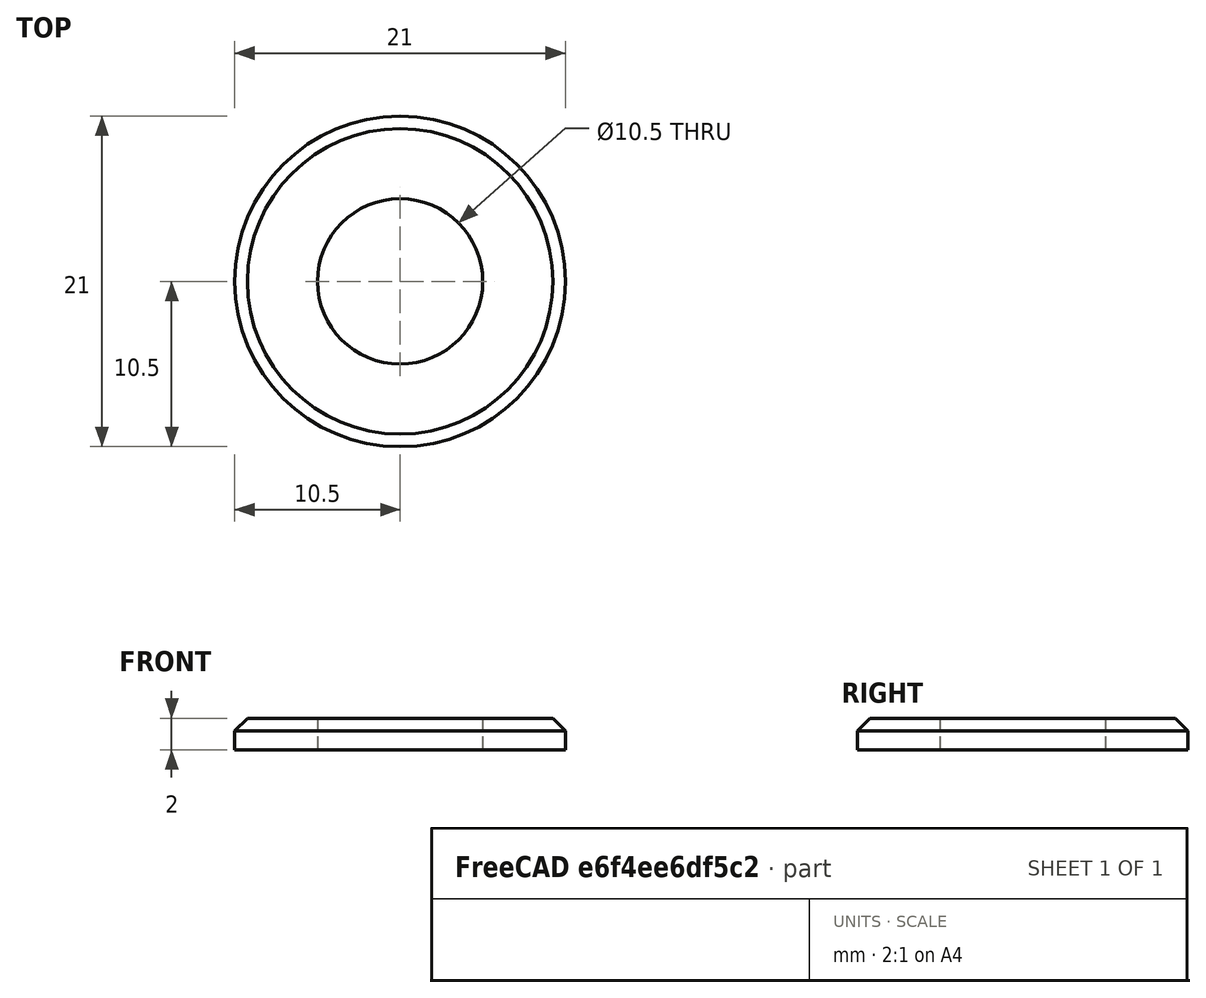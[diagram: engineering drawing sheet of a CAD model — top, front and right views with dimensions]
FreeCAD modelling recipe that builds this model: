
FCSTD DOCUMENT  (FreeCAD 0.15R4651 (Git))
Label: Scheibe_DIN125-B 10,5
License: CC-BY 3.0
LicenseURL: http://creativecommons.org/licenses/by/3.0/
objects: Sketcher::SketchObject×1, PartDesign::Revolution×1
note: 3 computed .brp shape members not serialized (recipe doc carries the construction recipe); baked Part::Feature solids carry a one-line shape summary decoded from their .brp

FEATURE [Sketcher::SketchObject] Sketch
  Placement = pos=(0,0,0) rot=(0.57735,0.57735,0.57735;2.0944rad)
  sketch-geometry (5):
    g0: LineSegment StartX=5.25 StartY=0 StartZ=0 EndX=10.5 EndY=0 EndZ=0
    g1: LineSegment StartX=10.5 StartY=0 StartZ=0 EndX=10.5 EndY=1.2 EndZ=0
    g2: LineSegment StartX=9.7 StartY=2 StartZ=0 EndX=5.25 EndY=2 EndZ=0
    g3: LineSegment StartX=5.25 StartY=2 StartZ=0 EndX=5.25 EndY=0 EndZ=0
    g4: LineSegment StartX=9.7 StartY=2 StartZ=0 EndX=10.5 EndY=1.2 EndZ=0
  constraints (15):
    c: Coincident(g0,g1)
    c: Coincident(g2,g3)
    c: Coincident(g3,g0)
    c: Horizontal(g0)
    c: Horizontal(g2)
    c: Vertical(g1)
    c: Vertical(g3)
    c: PointOnObject(g0,g-1)
    c: DistanceX(g-1,g2) = 5.25
    c: Coincident(g1,g4)
    c: Coincident(g2,g4)
    c: DistanceX(g-1,g1) = 10.5
    c: DistanceY(g3) = -2
    c: DistanceX(g4) = 0.8
    c: DistanceY(g4) = -0.8
FEATURE [PartDesign::Revolution] Revolution  label="Scheibe DIN 125 - B 10,5 #"
  Angle = 360
  Axis = (0,0,1)
  Base = (0,0,0)
  Placement = pos=(0,0,0) rot=(0.57735,0.57735,0.57735;2.0944rad)
  ReferenceAxis = -> Sketch [V_Axis]
  Reversed = true
  Sketch = -> Sketch
